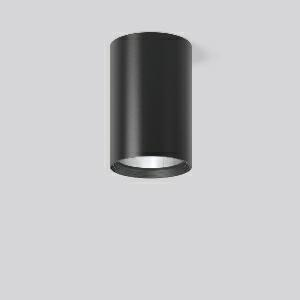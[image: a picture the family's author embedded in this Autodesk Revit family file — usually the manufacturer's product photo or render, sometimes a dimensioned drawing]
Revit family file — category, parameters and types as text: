
# Revit family: heledon_maxi_a_931224_003_1_4b29
name_source: partatom
category: Lighting Fixtures
units: mm (PartAtom-declared; Revit-internal decimal feet)

## family parameters
Cut with Voids When Loaded = No
Host = Face
Light Source = No
Part Type = Normal
Room Calculation Point = No
Round Connector Dimension = Use Diameter
Shared = No

## types (1)
- HELEDON maxi A (1 x LED Modul 940, 4550 lm, 4000)
    Apparent Load = 35 VA
    Approval mark = CE
    CIE Flux Codes = 100 100 100 100 100
    Color Rendering = 92
    Color Temperature = 4000
    Default Elevation = 1800 mm
    Description = Series: HELEDON maxi
Cylindrical surface-mounted downlight. Housing: die-cast aluminium, powder-coated. Internal ceiling frame polycarbonate with bayonet mounting. Black plastic ring and recessed LED to prevent glare from the side. Optical assembly with reflector made of MIRO-Silver with 98% total light reflection for outstanding efficiency - can be changed without tools. Best colour rendering index Ra>90. Suitable for Ceiling mounting. Easy installation with a separate ceiling frame with bayonet mounting and plug connection. Driver integrated. Connected via plug-in connector. High quality converter without flickering and stroboscopic effect. The following accessories can be mounted without use of tools: interchangeable lenses, decorative glasses, honeycomb louvre, clear and frosted diffusers, white interchangeable plastic ring. 
Colour: deep black, matt (RAL 9005)
Diameter: 123 mm
Height: 183 mm
Lamp: LED
Socket: without socket
Colour temperature: 4000K
Colour rendering index (CRI): 92
System power: 35 W
Rated luminous flux: 4550 lm
Luminous efficiency: 130 lm/W
Control gear: Regulated power supply
Protection class: I
Type of protection: IP 20
    Height = 183 mm
    Lamp = 1 x LED Modul 940
    Lamp Light Flux = 4550 lm
    Lamp count = 1
    Length = 123 mm
    Lifetime = 50000 h
    Luminous efficacy = 130 lm/W
    Manufacturer = RZB
    ModVariant = No
    Model = 931224.003.1
    Mounting Place = Ceiling
    Mounting Type = Surface mounted
    Number of Poles = 1
    OnlyDefault = Yes
    Power Factor = 1
    Product Name = HELEDON maxi A
    Product group = Surface mounted downlights
    ProductGroupID = 302
    Protection Class = Protection class I
    Protection Degree = IP 20
    RLX_Detail_Level = 1
    RLX_Emergency_Light_Flux = 0 lm
    RLX_Emergency_Type = 0
    RLX_Emergency_Type_DB = No
    RlxData = <blob elided: 99629 chars, md5=4a90822c>
    Socket = socket
    Standby Power = 0 W
    System Light Flux = 4550 lm
    System Power = 35 W
    Type Comments = Product without accessories
    Type Image = 931192.003.jpg
    URL = http://relux.com
    VarID = ---
    Voltage = 230 V
    Voltage Range = 220-240 V
    Weight = 0.00 kg
    Width = 0 mm  [stored 0 ft]

note: [stored X ft] marks values corroborated as IEEE doubles in the binary element streams (Revit-internal decimal feet)

## geometry (parser evidence)
native form markers: Blend x4, Sweep x11
no freeform markers — native parametric forms only
